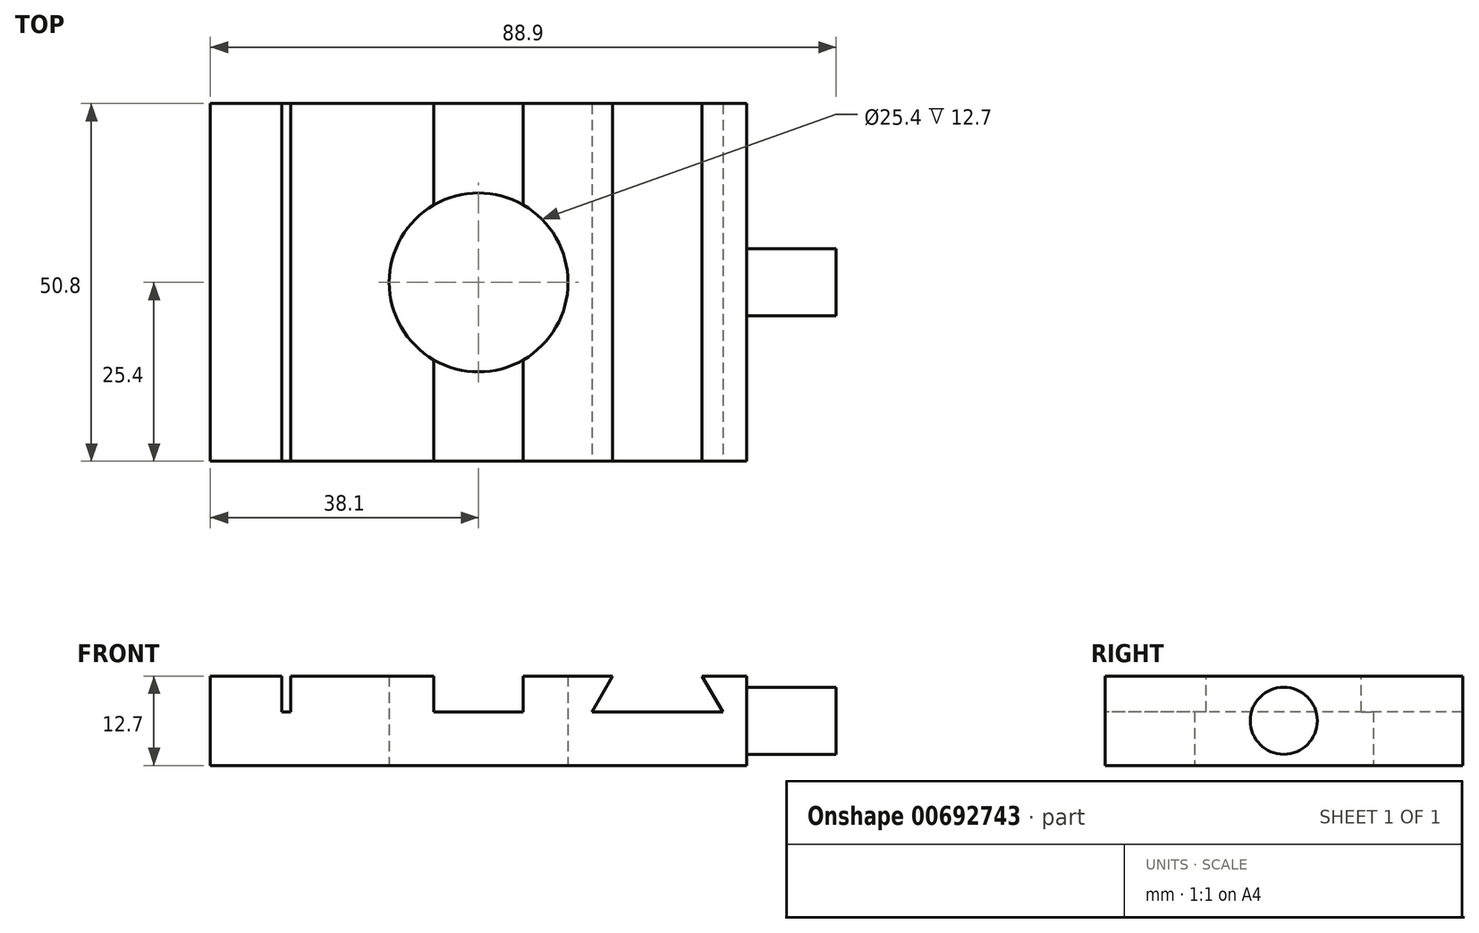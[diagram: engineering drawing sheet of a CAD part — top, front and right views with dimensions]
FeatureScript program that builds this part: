
annotation { "Feature Type Name" : "Feature", "Feature Type Description" : "" }
export const myFeature = defineFeature(function(context is Context, id is Id, definition is map)
    precondition{}
    {
        {
            var Q0;
            Q0=qCreatedBy(makeId("Top.planeOp"),FACE);
            var sketch = newSketch(context, id + "F0", { "sketchPlane" : qUnion([Q0])});
            skLineSegment(sketch, "E0.bottom", {"start": v(38.1, -25.4) * mm, "end": v(-38.1, -25.4) * mm});
            skLineSegment(sketch, "E0.top", {"start": v(38.1, 25.4) * mm, "end": v(-38.1, 25.4) * mm});
            skLineSegment(sketch, "E0.left", {"start": v(38.1, -25.4) * mm, "end": v(38.1, 25.4) * mm});
            skLineSegment(sketch, "E0.right", {"start": v(-38.1, -25.4) * mm, "end": v(-38.1, 25.4) * mm});
            skPoint(sketch, "E0.middle", {"position": v(0, 0) * mm});
            skCircle(sketch, "E1", {"center": v(0, 0) * mm, "radius": 12.7 * mm});
            skSolve(sketch);
        }
        {
            var Q0;
            Q0=makeQuery(id+"F0.imprint","IMPRINT",FACE,{"disambiguationData":[TD([[makeQuery(id+"F0.imprint","IMPRINT",EDGE,{"derivedFrom":sQuery(id+"F0.wireOp",EDGE,"E0.bottom")}),-1.0]])]});
            extrude(context, id + "F1", {"entities" : qUnion([Q0]), "depth" : 12.7 * mm, "offsetDistance" : 25 * mm});
        }
        {
            var Q0;
            Q0=makeQuery(id+"F1.opExtrude","CAP_FACE",FACE,{"disambiguationData":[OSD([sQuery(id+"F0.wireOp",EDGE,"E0.bottom"),sQuery(id+"F0.wireOp",EDGE,"E0.top"),sQuery(id+"F0.wireOp",EDGE,"E0.left"),sQuery(id+"F0.wireOp",EDGE,"E0.right"),sQuery(id+"F0.wireOp",EDGE,"E1")])],"isStart":false});
            var sketch = newSketch(context, id + "F2", { "sketchPlane" : qUnion([Q0])});
            skLineSegment(sketch, "E2.bottom", {"start": v(-27.94, 25.4) * mm, "end": v(-26.67, 25.4) * mm});
            skLineSegment(sketch, "E2.top", {"start": v(-27.94, -25.4) * mm, "end": v(-26.67, -25.4) * mm});
            skLineSegment(sketch, "E2.left", {"start": v(-27.94, 25.4) * mm, "end": v(-27.94, -25.4) * mm});
            skLineSegment(sketch, "E2.right", {"start": v(-26.67, 25.4) * mm, "end": v(-26.67, -25.4) * mm});
            skLineSegment(sketch, "E3", {"start": v(-6.35, 25.4) * mm, "end": v(-6.35, -25.4) * mm});
            skLineSegment(sketch, "E4", {"start": v(-6.35, -25.4) * mm, "end": v(6.35, -25.4) * mm});
            skLineSegment(sketch, "E5", {"start": v(6.35, -25.4) * mm, "end": v(6.35, 25.4) * mm});
            skLineSegment(sketch, "E6", {"start": v(6.35, 25.4) * mm, "end": v(-6.35, 25.4) * mm});
            skPoint(sketch, "E7", {"position": v(0, 0) * mm});
            skLineSegment(sketch, "E8", {"start": v(0, 25.4) * mm, "end": v(0, -25.4) * mm, "construction": true});
            skSolve(sketch);
        }
        {
            var Q0;
            Q0=makeQuery(id+"F2.imprint","IMPRINT",FACE,{"disambiguationData":[TD([[makeQuery(id+"F2.imprint","IMPRINT",EDGE,{"derivedFrom":sQuery(id+"F2.wireOp",EDGE,"E2.bottom")}),1.0]])]});
            var Q1;
            {var subQ0=sQuery(id+"F2.wireOp",EDGE,"E4");Q1=makeQuery(id+"F2.imprint","IMPRINT",FACE,{"disambiguationData":[TD([[makeQuery(id+"F2.imprint","IMPRINT",EDGE,{"derivedFrom":subQ0}),-1.0]])]});}
            var Q2;
            {var subQ0=sQuery(id+"F2.wireOp",EDGE,"E6");Q2=makeQuery(id+"F2.imprint","IMPRINT",FACE,{"disambiguationData":[TD([[makeQuery(id+"F2.imprint","IMPRINT",EDGE,{"derivedFrom":subQ0}),1.0]])]});}
            extrude(context, id + "F3", {"entities" : qUnion([Q0, Q1, Q2]), "operationType" : NewBodyOperationType.REMOVE, "oppositeDirection" : true, "depth" : 5.08 * mm, "offsetDistance" : 25.4 * mm});
        }
        {
            var Q0;
            Q0=makeQuery(id+"F1.opExtrude","SWEPT_FACE",FACE,{"disambiguationData":[OSD([sQuery(id+"F0.wireOp",EDGE,"E0.bottom")])]});
            var sketch = newSketch(context, id + "F4", { "sketchPlane" : qUnion([Q0])});
            skLineSegment(sketch, "E9", {"start": v(19.05, 12.7) * mm, "end": v(16.12, 7.62) * mm});
            skLineSegment(sketch, "E10", {"start": v(16.12, 7.62) * mm, "end": v(34.68, 7.62) * mm});
            skLineSegment(sketch, "E11", {"start": v(34.68, 7.62) * mm, "end": v(31.75, 12.7) * mm});
            skLineSegment(sketch, "E12", {"start": v(31.75, 12.7) * mm, "end": v(19.05, 12.7) * mm});
            skLineSegment(sketch, "E13", {"start": v(25.4, 12.7) * mm, "end": v(25.4, 7.62) * mm, "construction": true});
            skSolve(sketch);
        }
        {
            var Q0;
            Q0=makeQuery(id+"F4.imprint","IMPRINT",FACE,{"disambiguationData":[TD([[makeQuery(id+"F4.imprint","IMPRINT",EDGE,{"derivedFrom":sQuery(id+"F4.wireOp",EDGE,"E9")}),1.0]])]});
            extrude(context, id + "F5", {"entities" : qUnion([Q0]), "operationType" : NewBodyOperationType.REMOVE, "endBound" : BoundingType.THROUGH_ALL, "oppositeDirection" : true, "depth" : 25.4 * mm, "offsetDistance" : 25.4 * mm});
        }
        {
            var Q0;
            Q0=makeQuery(id+"F1.opExtrude","SWEPT_FACE",FACE,{"disambiguationData":[OSD([sQuery(id+"F0.wireOp",EDGE,"E0.left")])]});
            var sketch = newSketch(context, id + "F6", { "sketchPlane" : qUnion([Q0])});
            skCircle(sketch, "E14", {"center": v(0, 6.35) * mm, "radius": 4.76 * mm});
            skPoint(sketch, "E14.centerSnap0", {"position": v(-25.4, 6.35) * mm});
            skPoint(sketch, "E14.centerSnap1", {"position": v(0, 12.7) * mm});
            skSolve(sketch);
        }
        {
            var Q0;
            Q0 = qSketchRegion(id + "F6", true);
            extrude(context, id + "F7", {"entities" : qUnion([Q0]), "operationType" : NewBodyOperationType.ADD, "depth" : 12.7 * mm, "offsetDistance" : 25.4 * mm});
        }
    });
